# Revit family: POLYEVO
name_source: partatom
category: Luminaires
units: mm (PartAtom-declared; Revit-internal decimal feet)

## family parameters
Cote de connecteur circulaire = Utiliser le diamètre
Couper avec des vides une fois chargée = Non
Hôte = Face
Numéro OmniClass = 23.80.70.11.17
Partagée = Non
Point de calcul de pièce = Oui
Source d'éclairage = Oui
Titre OmniClass = Specialized Lighting by Location or Use
Type d'élément = Normal

## types (24) — shared parameters
Angle de l'inclinaison = 60.00°
Diamètre = 320 mm  [stored 1.04987 ft]
Emettre la visibilité des formes dans le rendu = Non
Emettre à partir du diamètre du cercle = 610 mm
Fabricant = Résistex
Filtre de couleur = 16777215
Garantie = 5 ans
Gradation des changements de température de couleur de lampe = <Aucun>
IK = 10
IP = 65
Image du type = <Aucun>
Indice de charge = Eclairage
Matériau diffuseur = PC Transparent
Modèle = Polyevo
Nombre pôles = 1
Tension = 230 V
URL = https://www.resistex-sa.com
Épaisseur = 74 mm  [stored 0.242782 ft]
Épaisseur côté = 1 mm  [stored 0.00328084 ft]
zero-valued in all types: Elévation par défaut

## per-type parameters (varying)
| type | Charge apparente | Commentaires relatifs à la puissance | Coût | Description | Fichier de distribution photométrique | Matériau corps |
| ON/OFF 4000K BLANC 883001 | 27 VA | 25.8W | 122.5 $ | Hublot équipé d'une platine LED SMD, efficacité lumineuse de 128.4lm/W | 883001.ies | PC Blanc |
| DÉTEC HF 4000K BLANC 883002 | 32 VA | 26.8W | 150 $ | Hublot équipé d'une platine LED SMD, efficacité lumineuse de 123.6lm/W | 883002.ies | PC Blanc |
| DÉTEC HF PRÉAVIS DEXTNCTION BLUETOOTH 4000K BLANC 883004 | 30 VA | 26.8W | 287.5 $ | Hublot équipé d'une platine LED SMD et d'une détection hyperfréquence pilotée avec préavis d'extinction paramétrable par Bluetooth, efficacité lumineuse de 123.6lm/W | 883004.ies | PC Blanc |
| ON/OFF 4000K GRAPHITE 883005 | 28 VA | 26W | 122.5 $ | Hublot équipé d'une platine LED SMD, efficacité lumineuse de 113lm/W | 883005.ies | PC Graphite |
| DÉTEC HF 4000K GRAPHITE 883006 | 32 VA | 27W | 150 $ | Hublot équipé d'une platine LED SMD et d'une détection hyperfréquences paramétrable par micro-switch, efficacité lumineuse de 108.9lm/W | 883006.ies | PC Graphite |
| DÉTEC HF PRÉAVIS DEXTNCTION BLUETOOTH 4000K GRAPHITE 883008 | 30 VA | 27W | 287.5 $ | Hublot équipé d'une platine LED SMD et d'une détection hyperfréquence pilotée avec préavis d'extinction paramétrable par Bluetooth, efficacité lumineuse de 108.9lm/W | 883008.ies | PC Graphite |
| ON/OFF 3000K BLANC 883009 | 27 VA | 25.7W | 122.5 $ | Hublot équipé d'une platine LED SMD, efficacité lumineuse de 119lm/W | 883009.ies | PC Blanc |
| DÉTEC HF 3000K BLANC 883010 | 31 VA | 26.7W | 150 $ | Hublot équipé d'une platine LED SMD et d'une détection hyperfréquences paramétrable par micro-switch, efficacité lumineuse de 114.7lm/W | 883010.ies | PC Blanc |
| DÉTEC HF PRÉAVIS DEXTNCTION BLUETOOTH 3000K BLANC 883012 | 30 VA | 26.7W | 287.5 $ | Hublot équipé d'une platine LED SMD et d'une détection hyperfréquence pilotée avec préavis d'extinction paramétrable par Bluetooth, efficacité lumineuse de 114.7lm/W | 883012.ies | PC Blanc |
| ON/OFF 3000K GRAPHITE 883013 | 28 VA | 25.9W | 122.5 $ | Hublot équipé d'une platine LED SMD, efficacité lumineuse de 105lm/W | 883013.ies | PC Graphite |
| DÉTEC HF 3000K GRAPHITE 883014 | 32 VA | 26.9W | 150 $ | Hublot équipé d'une platine LED SMD et d'une détection hyperfréquences paramétrable par micro-switch, efficacité lumineuse de 101lm/W | 883014.ies | PC Graphite |
| DÉTEC HF PRÉAVIS DEXTNCTION BLUETOOTH 3000K GRAPHITE 883016 | 30 VA | 26.9W | 287.5 $ | Hublot équipé d'une platine LED SMD et d'une détection hyperfréquence pilotée avec préavis d'extinction paramétrable par Bluetooth, efficacité lumineuse de 101lm/W | 883016.ies | PC Graphite |
| DALI 4000K GRAPHITE 883017 | 27 VA | 25.8W | 180 $ | Hublot équipé d'une platine LED SMD et d'un driver à commande DALI, efficacité lumineuse de 113lm/W | 883017.ies | PC Graphite |
| DÉTEC HF PRÉAVIS DEXTNCTION 4000K BLANC 883020 | 30 VA | 26.8W | 187.5 $ | Hublot équipé d'une platine LED SMD et d'une détection hyperfréquences avec préavis d'extinction paramétrable par switch, efficacité lumineuse de 123.6lm/W | 883020.ies | PC Blanc |
| DÉTEC HF PRÉAVIS DEXTNCTION 3000K BLANC 883021 | 30 VA | 26.7W | 187.5 $ | Hublot équipé d'une platine LED SMD et d'une détection hyperfréquences avec préavis d'extinction paramétrable par télécommande, efficacité lumineuse de 114.7lm/W | 883021.ies | PC Blanc |
| DÉTEC HF PRÉAVIS DEXTNCTION 4000K GRAPHITE 883022 | 30 VA | 27W | 187.5 $ | Hublot équipé d'une platine LED SMD et d'une détection hyperfréquences avec préavis d'extinction paramétrable par télécommande, efficacité lumineuse de 108.9lm/W | 883022.ies | PC Graphite |
| DÉTEC HF PRÉAVIS DEXTNCTION 3000K GRAPHITE 883023 | 30 VA | 26.9W | 187.5 $ | Hublot équipé d'une platine LED SMD et d'une détection hyperfréquences avec préavis d'extinction paramétrable par télécommande, efficacité lumineuse de 101lm/W | 883023.ies | PC Graphite |
| DALI 4000K BLANC 883025 | 27 VA | 25.8W | 180 $ | Hublot équipé d'une platine LED SMD et d'un driver à commande DALI, efficacité lumineuse de 128.4lm/W | 883025.ies | PC Blanc |
| DALI 3000K BLANC 883026 | 27 VA | 25.7W | 180 $ | Hublot équipé d'une platine LED SMD et d'un driver à commande DALI, efficacité lumineuse de 119lm/W | 883026.ies | PC Blanc |
| DALI 3000K GRAPHITE 883027 | 28 VA | 25.9W | 180 $ | Hublot équipé d'une platine LED SMD et d'un driver à commande DALI, efficacité lumineuse de 105lm/W | 883027.ies | PC Graphite |
| DÉTEC BLUETOOTH 3000K BLANC 883028 | 31 VA | 26.7W | 230 $ | Hublot équipé d'une platine LED SMD et d'une détection hyperfréquences paramétrable par Bluetooth, efficacité lumineuse de 114.7lm/W | 883028.ies | PC Blanc |
| DÉTEC BLUETOOTH 4000K BLANC 883029 | 32 VA | 26.8W | 230 $ | Hublot équipé d'une platine LED SMD et d'une détection hyperfréquences paramétrable par Bluetooth, efficacité lumineuse de 123.6lm/W | 883029.ies | PC Blanc |
| DÉTEC BLUETOOTH 3000K GRAPHITE 883030 | 32 VA | 26.9W | 230 $ | Hublot équipé d'une platine LED SMD et d'une détection hyperfréquences paramétrable par Bluetooth, efficacité lumineuse de 101lm/W | 883030.ies | PC Graphite |
| DÉTEC BLUETOOTH 4000K GRAPHITE 883031 | 32 VA | 27W | 230 $ | Hublot équipé d'une platine LED SMD et d'une détection hyperfréquences paramétrable par Bluetooth, efficacité lumineuse de 108.9lm/W | 883031.ies | PC Graphite |

note: [stored X ft] marks values corroborated as IEEE doubles in the binary element streams (Revit-internal decimal feet)
